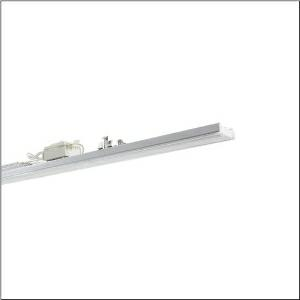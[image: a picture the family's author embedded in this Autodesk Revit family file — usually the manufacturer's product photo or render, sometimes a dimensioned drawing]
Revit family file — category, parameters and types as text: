
# Revit family: licross_21_recessed_ho_52tl12dn5e5m
name_source: partatom
category: Lighting Fixtures
units: mm (PartAtom-declared; Revit-internal decimal feet)

## family parameters
Cut with Voids When Loaded = No
Host = Face
Light Source = No
Part Type = Normal
Room Calculation Point = No
Round Connector Dimension = Use Diameter
Shared = No

## types (1)
- --- (1 x LED, 14860 lm, 84.6 W, 5000K)
    Apparent Load = 85 VA
    CIE Flux Codes = 69 91 98 100 100
    Color Rendering = 80
    Color Temperature = 5000K
    Default Elevation = 1800 mm
    Description = Licross 21 Recessed HO, luminaire insert, of sheet steel, galvanised, coil coated, white, length: 1.500mm, width: 66mm, height: 67mm, LED rated luminous flux: 14.860lm, light colour: 850, SDCM (Standard Deviation of Colour Matching)MacAdam ≤ 3 SDCM (initial), control gear: DALI 2, with plug, 5-pole, with phase selection, mains connection: 220..240V, AC, 50/60Hz, rated input power: 85W, internal wiring halogen-free, primary optical cover: cover, of PMMA, light emission: direct distribution, primary light characteristic: symmetric, protection rating (complete): IP40, insulation class (complete): insulation class I (protective earthing), certification: CE, ENEC, VDE, UKCA, protection symbol: D if used in an environment without relevant dust loads with corresponding accessories, impact resistance: IK06, permissible ambient temperature for indoor applications: -25..+30°C, corresponds to IFS (International Featured Standards) requirements for safety and quality in the food industry, reducing of maximum allowable ambient temperature of 5°C with ceiling mounting, LABS conformity tested according to VDMA 24364:2018-05, The light source and the operating device comply with the requirements of the Ecodesign Regulation (EU) 2019/2020 and are replaceable in accordance with this regulation, packaging unit: 1 piece
    Height = 58 mm
    Lamp = 1 x LED
    Lamp Light Flux = 14860 lm
    Lamp Power = 84.6 W
    Lamp count = 1
    Length = 1500 mm
    Luminous efficacy = 176 lm/W
    Manufacturer = Siteco
    ModVariant = No
    Model = 52TL12DN5E5M
    Mounting Place = Ceiling
    Mounting Type = Pendant
    Number of Poles = 1
    OnlyDefault = Yes
    Power Factor = 1
    Product Name = Licross 21 Recessed HO
    Product group = luminaire insert | ceiling pendant
    ProductGroupID = 901
    Protection Class = Protection class I
    Protection Degree = IP 40
    RLX_Detail_Level = 1
    RLX_Emergency_Light_Flux = 0 lm
    RLX_Emergency_Type = 0
    RLX_Emergency_Type_DB = No
    RlxData = <blob elided: 25009 chars, md5=2c2df052>
    Socket = socket
    Standby Power = 0 W
    System Light Flux = 14860 lm
    System Power = 85 W
    Type Comments = factory setting: luminous flux: 100 % | dim-lin: 254 | 484 mA
    Type Image = l_1296930.jpg
    URL = http://relux.com
    VarID = @adj_092867
    Voltage = 0 V
    Weight = 0.00 kg
    Width = 66 mm

## geometry (parser evidence)
native form markers: Blend x4, Sweep x12
no freeform markers — native parametric forms only
